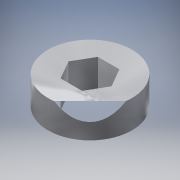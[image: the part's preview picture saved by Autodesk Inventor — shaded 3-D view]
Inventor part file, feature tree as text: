
AUTODESK INVENTOR PART (.ipt)
format: ipt  version: 2016 (Build 200138000, 138)  size: 103,936 bytes
history: native  units: in
note: dims shown in document units (in); Inventor stores cm internally (conversion verified against a paired STEP export)
features: extrude x1, sketch x1
ambient origin geometry x8: Origin, YZ Plane, XZ Plane, XY Plane, X Axis, Y Axis, Z Axis, Center Point
bodies: Solid1 (feature_tree)
feature tree (2):
  extrude  "Extrusion1"  Depth=0.5in
  sketch  "Sketch1"  dims[d0=1.125in d1=0.5in d2=0.375in d3=0.0in]
